# Revit family: CONTURA II CF WH INV2 SUITE GG
name_source: partatom
category: Specialty Equipment
units: mm (PartAtom-declared; Revit-internal decimal feet)

## family parameters
Cut with Voids When Loaded = No
Host = Face
OmniClass Number = 23.45.05.21.11.11
OmniClass Title = Water Operated Water Closets
Part Type = Normal
Room Calculation Point = No
Round Connector Dimension = Use Radius
Shared = No

## types (3) — shared parameters
Assembly Code = D2010110
Manufacturer = GWA Bathrooms & Kitchens
Material_Buttons = GWA_Metal-Chrome
Material_Fixing = GWA_Metal-Stainless
Material_Seat = GWA-Acrylic-White
URL = https://www.caroma.com.au
zero-valued in all types: Default Elevation

## per-type parameters (varying)
| type | Description | Material_Base | Model |
| CONTURA II CF WH INV2 SUITE GG - MATTE WHITE | CONTURA II CF WH INV2 SUITE GG - MATTE WHITE | GWA-Porcelain-Matte-White | 849001MW |
| CONTURA II CF WH INV2 SUITE GG - MATTE CLAY | CONTURA II CF WH INV2 SUITE GG - MATTE CLAY | GWA-Porcelain-Matte-Clay | 849001CL |
| CONTURA II CF WH INV2 SUITE GG - WHITE | CONTURA II CF WH INV2 SUITE GG- WHITE | GWA-Porcelain-White | 849001W |

## geometry (parser evidence)
native form markers: Sweep x3
no freeform markers — native parametric forms only
